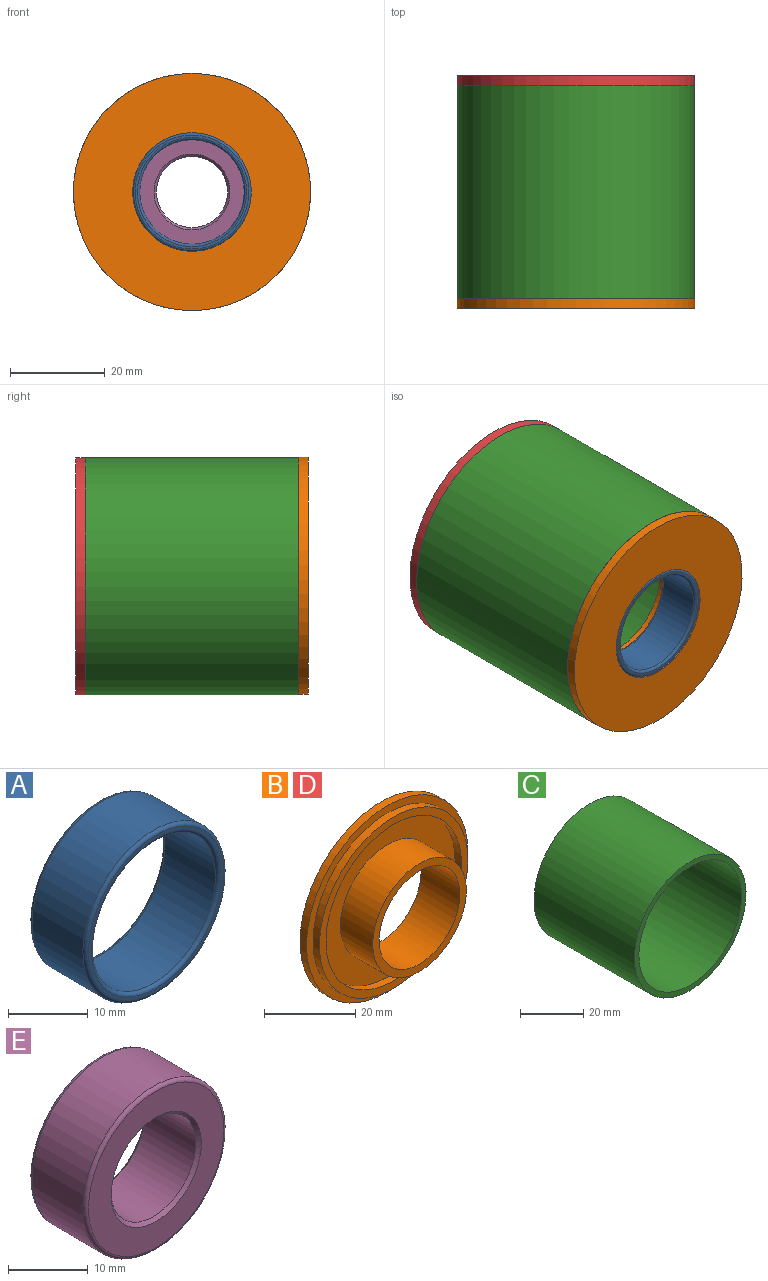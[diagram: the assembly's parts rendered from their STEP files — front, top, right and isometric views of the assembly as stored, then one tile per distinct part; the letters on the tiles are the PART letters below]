
ASSEMBLY  parts=5 mates=8
PART A: 8 faces, bbox 27.1x10x27.1 mm
  f0: cylinder r=11mm len=22mm, axis (0,1,0), area 622mm2, adj f4,f6
  f1: cylinder r=12.5mm len=25mm, axis (0,1,0), area 706.9mm2, adj f5,f7
  f2: plane 24x24mm, normal (0,-1,0), area 36.9mm2, adj f6,f7
  f3: plane 24x24mm, normal (0,1,0), area 36.9mm2, adj f4,f5
  f4: torus R=11.5mm, axis (0,-1,0), area 55.2mm2, adj f0,f3
  f5: torus R=12mm, axis (0,-1,0), area 60.8mm2, adj f1,f3
  f6: torus R=11.5mm, axis (0,-1,0), area 55.2mm2, adj f0,f2
  f7: torus R=12mm, axis (0,-1,0), area 60.8mm2, adj f1,f2
PART B: 10 faces, bbox 50x12x50 mm
  f0: cylinder r=25mm len=50mm, axis (0,1,0), area 314.2mm2, adj f1,f2
  f1: plane 50x50mm, normal (0,-1,0), area 301.6mm2, adj f0,f4
  f2: plane 50x50mm, normal (0,1,0), area 1472.6mm2, adj f0,f7
  f3: cylinder r=21mm len=42mm, axis (0,1,0), area 263.9mm2, adj f5,f6
  f4: cylinder r=23mm len=46mm, axis (0,1,0), area 289mm2, adj f1,f5
  f5: plane 46x46mm, normal (0,-1,0), area 276.5mm2, adj f3,f4
  f6: plane 42x42mm, normal (0,-1,0), area 724.9mm2, adj f3,f8
  f7: cylinder r=12.5mm len=25mm, axis (0,1,0), area 942.5mm2, adj f2,f9
  f8: cylinder r=14.5mm len=29mm, axis (0,1,0), area 911.1mm2, adj f6,f9
  f9: plane 29x29mm, normal (0,-1,0), area 169.6mm2, adj f7,f8
PART C: 4 faces, bbox 50x45x50 mm
  f0: cylinder r=23mm len=46mm, axis (0,1,0), area 6503.1mm2, adj f2,f3
  f1: cylinder r=25mm len=50mm, axis (0,1,0), area 7068.6mm2, adj f2,f3
  f2: plane 50x50mm, normal (0,-1,0), area 301.6mm2, adj f0,f1
  f3: plane 50x50mm, normal (0,1,0), area 301.6mm2, adj f0,f1
PART D: same geometry as B
PART E: 8 faces, bbox 27.1x10x27.1 mm
  f0: cylinder r=7.5mm len=15mm, axis (0,1,0), area 424.1mm2, adj f6,f7
  f1: cylinder r=12.5mm len=25mm, axis (0,1,0), area 706.9mm2, adj f4,f5
  f2: plane 24x24mm, normal (0,-1,0), area 251.3mm2, adj f5,f7
  f3: plane 24x24mm, normal (0,1,0), area 251.3mm2, adj f4,f6
  f4: torus R=12mm, axis (0,-1,0), area 60.8mm2, adj f1,f3
  f5: torus R=12mm, axis (0,-1,0), area 60.8mm2, adj f1,f2
  f6: cone r=8mm half-angle=45deg, axis (0,1,0), area 34.4mm2, adj f0,f3
  f7: cone r=7.5mm half-angle=45deg, axis (0,-1,0), area 34.4mm2, adj f0,f2
PLACE A t=(35.24,-13.45,-0.75)mm
PLACE B rot(axis=(1,0,0),180deg) t=(35.24,-23.45,-0.75)mm
PLACE C t=(35.24,23.55,-0.75)mm
PLACE D t=(35.24,25.55,-0.75)mm
PLACE E t=(35.24,25.55,-0.75)mm
MATE cylindrical C.f1 <-> D.f0  axis (0,1,0) through (35.24,23.55,-0.75)mm
MATE planar B.f0 <-> A.f1  axis (0,-1,0) through (35.24,-23.45,-0.75)mm
MATE planar C.f0 <-> D.f3  axis (0,1,0) through (35.24,23.55,-0.75)mm
MATE cylindrical B.f3 <-> A.f1  axis (0,1,0) through (35.24,-11.45,-0.75)mm
MATE planar C.f1 <-> B.f3  axis (0,-1,0) through (35.24,-21.45,-0.75)mm
MATE planar D.f3 <-> E.f0  axis (0,1,0) through (35.24,25.55,-0.75)mm
MATE cylindrical C.f1 <-> B.f0  axis (0,1,0) through (35.24,1.05,-0.75)mm
MATE cylindrical C.f1 <-> E.f1  axis (0,1,0) through (35.24,1.05,-0.75)mm
